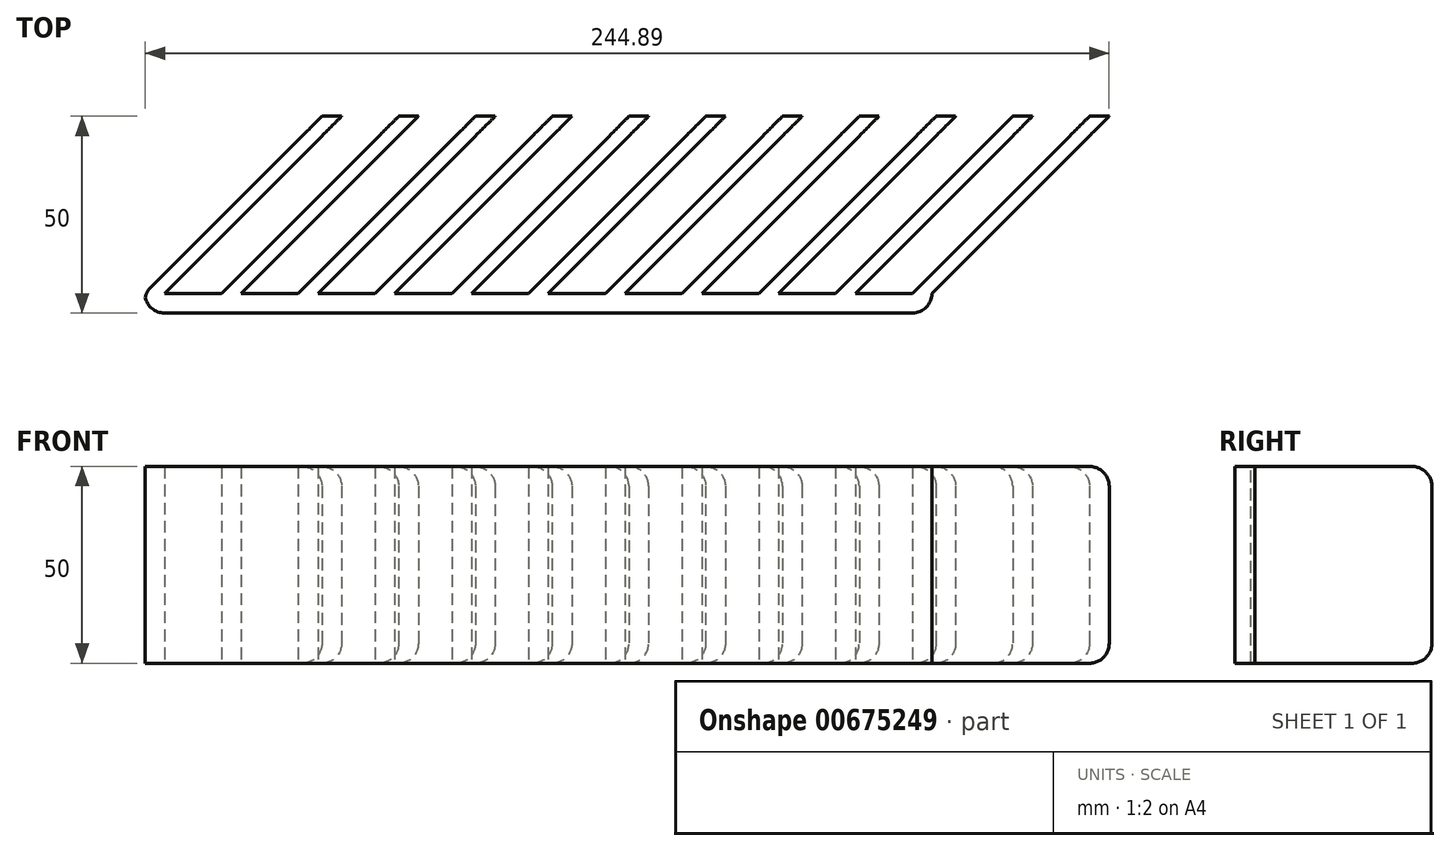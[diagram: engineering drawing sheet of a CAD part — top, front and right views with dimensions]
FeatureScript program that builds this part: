
annotation { "Feature Type Name" : "Feature", "Feature Type Description" : "" }
export const myFeature = defineFeature(function(context is Context, id is Id, definition is map)
    precondition{}
    {
        {
            var Q0;
            Q0=qCreatedBy(makeId("Top.planeOp"),FACE);
            var sketch = newSketch(context, id + "F0", { "sketchPlane" : qUnion([Q0])});
            skLineSegment(sketch, "E0.top", {"start": v(-96.18, -21) * mm, "end": v(103.82, -21) * mm});
            skLineSegment(sketch, "E1", {"start": v(-96.18, -16) * mm, "end": v(103.82, -16) * mm});
            skLineSegment(sketch, "E2", {"start": v(-96.18, -16) * mm, "end": v(-51.18, 29) * mm});
            skLineSegment(sketch, "E3", {"start": v(-91.18, -16) * mm, "end": v(-46.18, 29) * mm});
            skLineSegment(sketch, "E4", {"start": v(-76.68, -16) * mm, "end": v(-31.68, 29) * mm});
            skPoint(sketch, "E5.endSnap0", {"position": v(3.82, -16) * mm});
            skLineSegment(sketch, "E6", {"start": v(-71.68, -16) * mm, "end": v(-26.68, 29) * mm});
            skLineSegment(sketch, "E7", {"start": v(-57.18, -16) * mm, "end": v(-12.18, 29) * mm});
            skLineSegment(sketch, "E8", {"start": v(-52.18, -16) * mm, "end": v(-7.18, 29) * mm});
            skLineSegment(sketch, "E9", {"start": v(-37.68, -16) * mm, "end": v(7.32, 29) * mm});
            skLineSegment(sketch, "E10", {"start": v(-32.68, -16) * mm, "end": v(12.32, 29) * mm});
            skLineSegment(sketch, "E11", {"start": v(26.82, 29) * mm, "end": v(-18.18, -16) * mm});
            skLineSegment(sketch, "E12", {"start": v(1.32, -16) * mm, "end": v(46.32, 29) * mm});
            skLineSegment(sketch, "E13", {"start": v(31.82, 29) * mm, "end": v(-13.18, -16) * mm});
            skLineSegment(sketch, "E14", {"start": v(6.32, -16) * mm, "end": v(51.32, 29) * mm});
            skLineSegment(sketch, "E15", {"start": v(25.82, -16) * mm, "end": v(70.82, 29) * mm});
            skLineSegment(sketch, "E16", {"start": v(85.32, 29) * mm, "end": v(40.32, -16) * mm});
            skLineSegment(sketch, "E17", {"start": v(45.32, -16) * mm, "end": v(90.32, 29) * mm});
            skLineSegment(sketch, "E18", {"start": v(59.82, -16) * mm, "end": v(104.82, 29) * mm});
            skLineSegment(sketch, "E19", {"start": v(103.82, -16) * mm, "end": v(103.82, -21) * mm});
            skLineSegment(sketch, "E20", {"start": v(64.82, -16) * mm, "end": v(109.82, 29) * mm});
            skLineSegment(sketch, "E21", {"start": v(85.32, 29) * mm, "end": v(90.32, 29) * mm});
            skLineSegment(sketch, "E22", {"start": v(104.82, 29) * mm, "end": v(109.82, 29) * mm});
            skLineSegment(sketch, "E23", {"start": v(70.82, 29) * mm, "end": v(65.82, 29) * mm});
            skLineSegment(sketch, "E24", {"start": v(25.82, -16) * mm, "end": v(20.82, -16) * mm, "construction": true});
            skLineSegment(sketch, "E25", {"start": v(65.82, 29) * mm, "end": v(20.82, -16) * mm});
            skLineSegment(sketch, "E26", {"start": v(26.82, 29) * mm, "end": v(31.82, 29) * mm});
            skLineSegment(sketch, "E27", {"start": v(46.32, 29) * mm, "end": v(51.32, 29) * mm});
            skLineSegment(sketch, "E28", {"start": v(7.32, 29) * mm, "end": v(12.32, 29) * mm});
            skLineSegment(sketch, "E29", {"start": v(-12.18, 29) * mm, "end": v(-7.18, 29) * mm});
            skLineSegment(sketch, "E30", {"start": v(-31.68, 29) * mm, "end": v(-26.68, 29) * mm});
            skLineSegment(sketch, "E31", {"start": v(-51.18, 29) * mm, "end": v(-46.18, 29) * mm});
            skLineSegment(sketch, "E32", {"start": v(-96.18, -16) * mm, "end": v(-96.18, -21) * mm});
            skLineSegment(sketch, "E33", {"start": v(124.32, 29) * mm, "end": v(79.32, -16) * mm});
            skLineSegment(sketch, "E34", {"start": v(84.32, -16) * mm, "end": v(129.32, 29) * mm});
            skLineSegment(sketch, "E35", {"start": v(98.82, -16) * mm, "end": v(143.82, 29) * mm});
            skLineSegment(sketch, "E36", {"start": v(103.82, -16) * mm, "end": v(148.82, 29) * mm});
            skLineSegment(sketch, "E37", {"start": v(124.32, 29) * mm, "end": v(129.32, 29) * mm});
            skLineSegment(sketch, "E38", {"start": v(143.82, 29) * mm, "end": v(148.82, 29) * mm});
            skSolve(sketch);
        }
        {
            var Q0;
            Q0 = qSketchRegion(id + "F0", true);
            extrude(context, id + "F1", {"entities" : qUnion([Q0]), "endBound" : BoundingType.SYMMETRIC, "depth" : 50 * mm, "offsetDistance" : 25 * mm});
        }
        {
            var Q0;
            Q0=makeQuery(id+"F1.opExtrude","CAP_EDGE",EDGE,{"disambiguationData":[OSD([sQuery(id+"F0.wireOp",EDGE,"E31")])],"isStart":false});
            var Q1;
            Q1=makeQuery(id+"F1.opExtrude","CAP_EDGE",EDGE,{"disambiguationData":[OSD([sQuery(id+"F0.wireOp",EDGE,"E30")])],"isStart":false});
            var Q2;
            Q2=makeQuery(id+"F1.opExtrude","CAP_EDGE",EDGE,{"disambiguationData":[OSD([sQuery(id+"F0.wireOp",EDGE,"E29")])],"isStart":false});
            var Q3;
            Q3=makeQuery(id+"F1.opExtrude","CAP_EDGE",EDGE,{"disambiguationData":[OSD([sQuery(id+"F0.wireOp",EDGE,"E28")])],"isStart":false});
            var Q4;
            Q4=makeQuery(id+"F1.opExtrude","CAP_EDGE",EDGE,{"disambiguationData":[OSD([sQuery(id+"F0.wireOp",EDGE,"E26")])],"isStart":false});
            var Q5;
            Q5=makeQuery(id+"F1.opExtrude","CAP_EDGE",EDGE,{"disambiguationData":[OSD([sQuery(id+"F0.wireOp",EDGE,"E27")])],"isStart":false});
            var Q6;
            Q6=makeQuery(id+"F1.opExtrude","CAP_EDGE",EDGE,{"disambiguationData":[OSD([sQuery(id+"F0.wireOp",EDGE,"E23")])],"isStart":false});
            var Q7;
            Q7=makeQuery(id+"F1.opExtrude","CAP_EDGE",EDGE,{"disambiguationData":[OSD([sQuery(id+"F0.wireOp",EDGE,"E21")])],"isStart":false});
            var Q8;
            Q8=makeQuery(id+"F1.opExtrude","CAP_EDGE",EDGE,{"disambiguationData":[OSD([sQuery(id+"F0.wireOp",EDGE,"E22")])],"isStart":false});
            var Q9;
            Q9=makeQuery(id+"F1.opExtrude","CAP_EDGE",EDGE,{"disambiguationData":[OSD([sQuery(id+"F0.wireOp",EDGE,"E37")])],"isStart":false});
            var Q10;
            Q10=makeQuery(id+"F1.opExtrude","CAP_EDGE",EDGE,{"disambiguationData":[OSD([sQuery(id+"F0.wireOp",EDGE,"E38")])],"isStart":false});
            var Q11;
            Q11=makeQuery(id+"F1.opExtrude","CAP_EDGE",EDGE,{"disambiguationData":[OSD([sQuery(id+"F0.wireOp",EDGE,"E38")])],"isStart":true});
            var Q12;
            Q12=makeQuery(id+"F1.opExtrude","CAP_EDGE",EDGE,{"disambiguationData":[OSD([sQuery(id+"F0.wireOp",EDGE,"E37")])],"isStart":true});
            var Q13;
            Q13=makeQuery(id+"F1.opExtrude","CAP_EDGE",EDGE,{"disambiguationData":[OSD([sQuery(id+"F0.wireOp",EDGE,"E22")])],"isStart":true});
            var Q14;
            Q14=makeQuery(id+"F1.opExtrude","CAP_EDGE",EDGE,{"disambiguationData":[OSD([sQuery(id+"F0.wireOp",EDGE,"E21")])],"isStart":true});
            var Q15;
            Q15=makeQuery(id+"F1.opExtrude","CAP_EDGE",EDGE,{"disambiguationData":[OSD([sQuery(id+"F0.wireOp",EDGE,"E23")])],"isStart":true});
            var Q16;
            Q16=makeQuery(id+"F1.opExtrude","CAP_EDGE",EDGE,{"disambiguationData":[OSD([sQuery(id+"F0.wireOp",EDGE,"E27")])],"isStart":true});
            var Q17;
            Q17=makeQuery(id+"F1.opExtrude","CAP_EDGE",EDGE,{"disambiguationData":[OSD([sQuery(id+"F0.wireOp",EDGE,"E26")])],"isStart":true});
            var Q18;
            Q18=makeQuery(id+"F1.opExtrude","CAP_EDGE",EDGE,{"disambiguationData":[OSD([sQuery(id+"F0.wireOp",EDGE,"E28")])],"isStart":true});
            var Q19;
            Q19=makeQuery(id+"F1.opExtrude","CAP_EDGE",EDGE,{"disambiguationData":[OSD([sQuery(id+"F0.wireOp",EDGE,"E29")])],"isStart":true});
            var Q20;
            Q20=makeQuery(id+"F1.opExtrude","CAP_EDGE",EDGE,{"disambiguationData":[OSD([sQuery(id+"F0.wireOp",EDGE,"E30")])],"isStart":true});
            var Q21;
            Q21=makeQuery(id+"F1.opExtrude","CAP_EDGE",EDGE,{"disambiguationData":[OSD([sQuery(id+"F0.wireOp",EDGE,"E31")])],"isStart":true});
            var Q22;
            Q22=makeQuery(id+"F1.opExtrude","SWEPT_EDGE",EDGE,{"disambiguationData":[OSD([sQuery(id+"F0.wireOp",EDGE,"E1"),sQuery(id+"F0.wireOp",EDGE,"E2"),sQuery(id+"F0.wireOp",EDGE,"E32")])]});
            var Q23;
            Q23=makeQuery(id+"F1.opExtrude","SWEPT_EDGE",EDGE,{"disambiguationData":[OSD([sQuery(id+"F0.wireOp",EDGE,"E0.top"),sQuery(id+"F0.wireOp",EDGE,"E32")])]});
            var Q24;
            Q24=makeQuery(id+"F1.opExtrude","SWEPT_EDGE",EDGE,{"disambiguationData":[OSD([sQuery(id+"F0.wireOp",EDGE,"E0.top"),sQuery(id+"F0.wireOp",EDGE,"E19")])]});
            fillet(context, id + "F2", {"entities" : qUnion([Q0, Q1, Q2, Q3, Q4, Q5, Q6, Q7, Q8, Q9, Q10, Q11, Q12, Q13, Q14, Q15, Q16, Q17, Q18, Q19, Q20, Q21, Q22, Q23, Q24]), "radius" : 5 * mm, "tangentPropagation" : true, "allowEdgeOverflow" : false});
        }
    });
